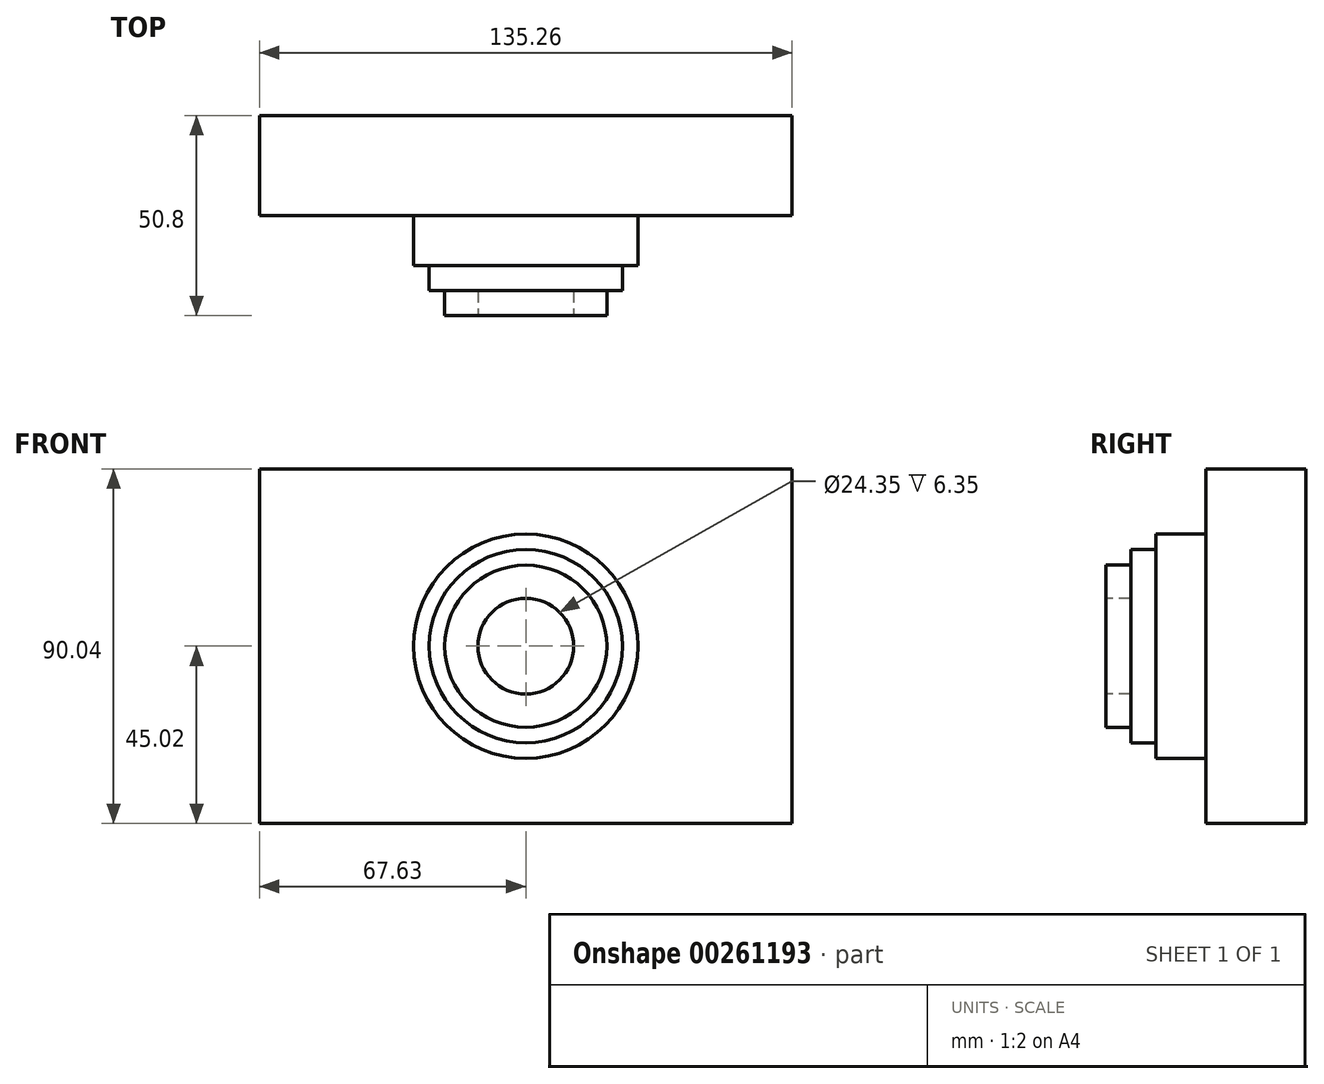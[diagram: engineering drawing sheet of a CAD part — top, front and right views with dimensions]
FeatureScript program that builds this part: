
annotation { "Feature Type Name" : "Feature", "Feature Type Description" : "" }
export const myFeature = defineFeature(function(context is Context, id is Id, definition is map)
    precondition{}
    {
        {
            var Q0;
            Q0=qCreatedBy(makeId("Front.planeOp"),FACE);
            var sketch = newSketch(context, id + "F0", { "sketchPlane" : qUnion([Q0])});
            skLineSegment(sketch, "E0.bottom", {"start": v(67.63, -45.02) * mm, "end": v(-67.63, -45.02) * mm});
            skLineSegment(sketch, "E0.top", {"start": v(67.63, 45.02) * mm, "end": v(-67.63, 45.02) * mm});
            skLineSegment(sketch, "E0.left", {"start": v(67.63, -45.02) * mm, "end": v(67.63, 45.02) * mm});
            skLineSegment(sketch, "E0.right", {"start": v(-67.63, -45.02) * mm, "end": v(-67.63, 45.02) * mm});
            skPoint(sketch, "E0.middle", {"position": v(0, 0) * mm});
            skSolve(sketch);
        }
        {
            var Q0;
            Q0 = qSketchRegion(id + "F0", true);
            extrude(context, id + "F1", {"entities" : qUnion([Q0]), "depth" : 25.4 * mm});
        }
        {
            var Q0;
            Q0=makeQuery(id+"F1.opExtrude","CAP_FACE",FACE,{"disambiguationData":[OSD([sQuery(id+"F0.wireOp",EDGE,"E0.bottom"),sQuery(id+"F0.wireOp",EDGE,"E0.top"),sQuery(id+"F0.wireOp",EDGE,"E0.left"),sQuery(id+"F0.wireOp",EDGE,"E0.right")])],"isStart":false});
            var sketch = newSketch(context, id + "F2", { "sketchPlane" : qUnion([Q0])});
            skCircle(sketch, "E1", {"center": v(0, 0) * mm, "radius": 20.59 * mm});
            skSolve(sketch);
        }
        {
            var Q0;
            Q0=qCreatedBy(makeId("Front.planeOp"),FACE);
            var sketch = newSketch(context, id + "F3", { "sketchPlane" : qUnion([Q0])});
            skCircle(sketch, "E2", {"center": v(0, 0) * mm, "radius": 10.44 * mm});
            skSolve(sketch);
        }
        {
            var Q0;
            Q0 = qSketchRegion(id + "F2", true);
            extrude(context, id + "F4", {"entities" : qUnion([Q0]), "operationType" : NewBodyOperationType.ADD, "depth" : 25.4 * mm});
        }
        {
            var Q0;
            Q0 = qSketchRegion(id + "F3", true);
            extrude(context, id + "F5", {"entities" : qUnion([Q0]), "operationType" : NewBodyOperationType.ADD, "depth" : 38.1 * mm});
        }
        {
            var Q0;
            Q0=makeQuery(id+"F4.opExtrude","CAP_FACE",FACE,{"disambiguationData":[OSD([sQuery(id+"F2.wireOp",EDGE,"E1")])],"isStart":false});
            var sketch = newSketch(context, id + "F6", { "sketchPlane" : qUnion([Q0])});
            skSolve(sketch);
        }
        {
            var Q0;
            Q0=makeQuery(id+"F6.imprint","IMPRINT",FACE,{"disambiguationData":[TD([[makeQuery(id+"F6.imprint","IMPRINT",EDGE,{"derivedFrom":makeQuery(id+"F4.opExtrude","CAP_EDGE",EDGE,{"disambiguationData":[OSD([sQuery(id+"F2.wireOp",EDGE,"E1")])],"isStart":false})}),1.0]])]});
            var sketch = newSketch(context, id + "F7", { "sketchPlane" : qUnion([Q0])});
            skCircle(sketch, "E3", {"center": v(0, 0) * mm, "radius": 12.18 * mm});
            skSolve(sketch);
        }
        {
            var Q0;
            Q0 = qSketchRegion(id + "F7", true);
            extrude(context, id + "F8", {"entities" : qUnion([Q0]), "operationType" : NewBodyOperationType.REMOVE, "oppositeDirection" : true, "depth" : 25.4 * mm});
        }
        {
            var Q0;
            Q0=makeQuery(id+"F1.opExtrude","CAP_FACE",FACE,{"disambiguationData":[OSD([sQuery(id+"F0.wireOp",EDGE,"E0.bottom"),sQuery(id+"F0.wireOp",EDGE,"E0.top"),sQuery(id+"F0.wireOp",EDGE,"E0.left"),sQuery(id+"F0.wireOp",EDGE,"E0.right")])],"isStart":false});
            var sketch = newSketch(context, id + "F9", { "sketchPlane" : qUnion([Q0])});
            skCircle(sketch, "E4", {"center": v(0, 0) * mm, "radius": 24.53 * mm});
            skSolve(sketch);
        }
        {
            var Q0;
            Q0 = qSketchRegion(id + "F9", true);
            extrude(context, id + "F10", {"entities" : qUnion([Q0]), "operationType" : NewBodyOperationType.ADD, "depth" : 19.05 * mm});
        }
        {
            var Q0;
            Q0=makeQuery(id+"F1.opExtrude","CAP_FACE",FACE,{"disambiguationData":[OSD([sQuery(id+"F0.wireOp",EDGE,"E0.bottom"),sQuery(id+"F0.wireOp",EDGE,"E0.top"),sQuery(id+"F0.wireOp",EDGE,"E0.left"),sQuery(id+"F0.wireOp",EDGE,"E0.right")])],"isStart":false});
            var sketch = newSketch(context, id + "F11", { "sketchPlane" : qUnion([Q0])});
            skCircle(sketch, "E5", {"center": v(0, 0) * mm, "radius": 28.48 * mm});
            skSolve(sketch);
        }
        {
            var Q0;
            Q0 = qSketchRegion(id + "F11", true);
            extrude(context, id + "F12", {"entities" : qUnion([Q0]), "operationType" : NewBodyOperationType.ADD, "depth" : 12.7 * mm});
        }
    });
